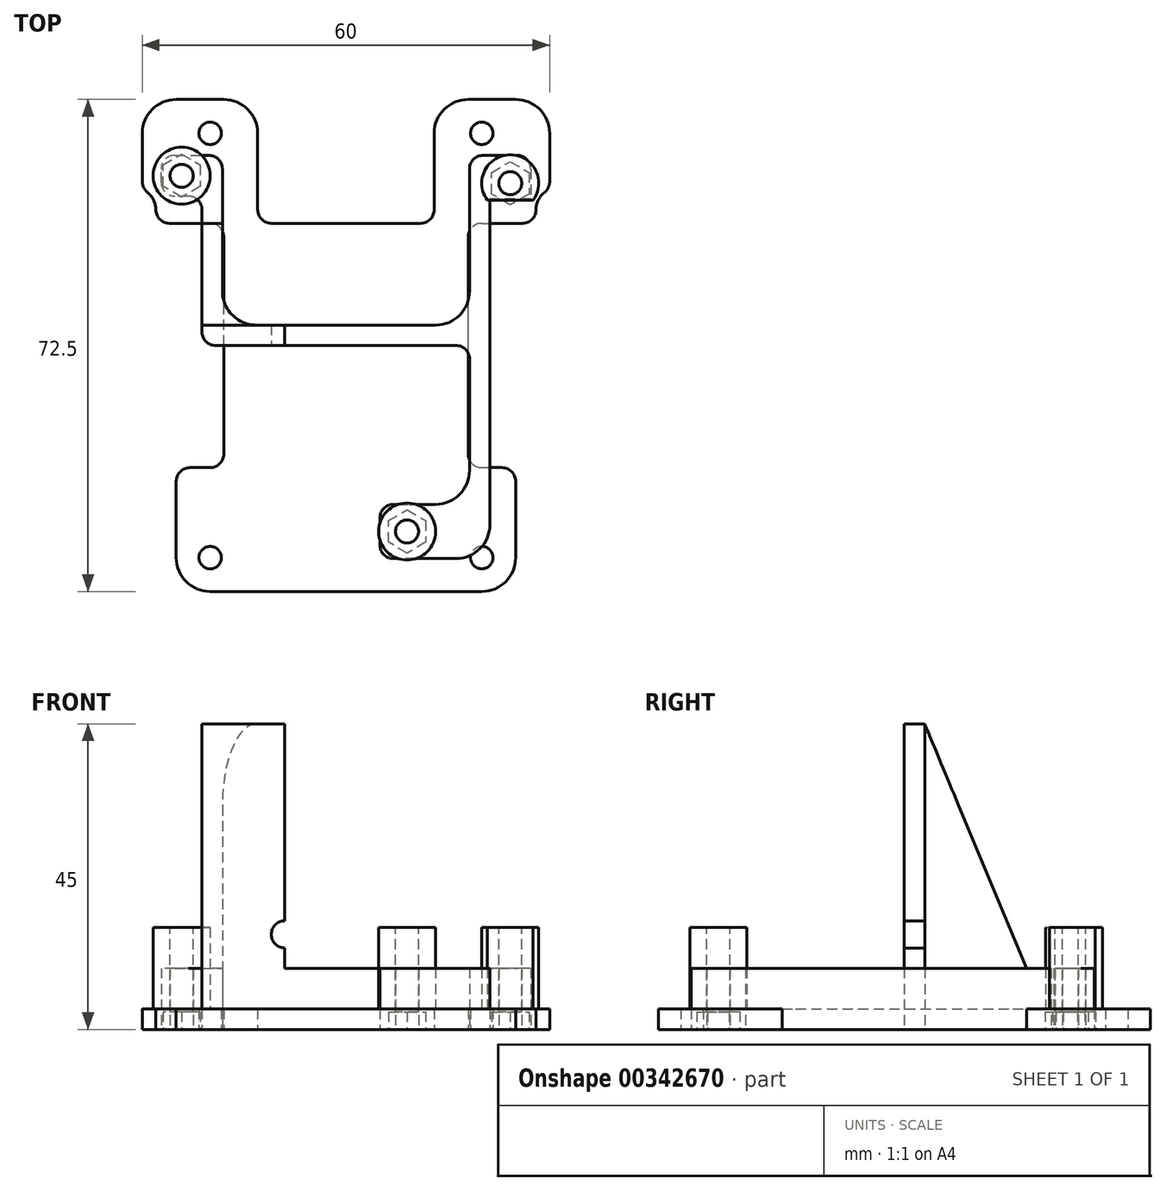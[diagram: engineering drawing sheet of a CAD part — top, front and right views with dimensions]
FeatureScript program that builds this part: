
annotation { "Feature Type Name" : "Feature", "Feature Type Description" : "" }
export const myFeature = defineFeature(function(context is Context, id is Id, definition is map)
    precondition{}
    {
        {
            var Q0;
            Q0=qCreatedBy(makeId("Top.planeOp"),FACE);
            var sketch = newSketch(context, id + "F0", { "sketchPlane" : qUnion([Q0])});
            skLineSegment(sketch, "E0.bottom", {"start": v(-35, -30) * mm, "end": v(35, -30) * mm, "construction": true});
            skLineSegment(sketch, "E0.top", {"start": v(-35, 52.5) * mm, "end": v(35, 52.5) * mm, "construction": true});
            skLineSegment(sketch, "E0.left", {"start": v(-35, -30) * mm, "end": v(-35, 52.5) * mm, "construction": true});
            skLineSegment(sketch, "E0.right", {"start": v(35, -30) * mm, "end": v(35, 52.5) * mm, "construction": true});
            skLineSegment(sketch, "E1", {"start": v(-35, 0) * mm, "end": v(35, 0) * mm, "construction": true});
            skCircle(sketch, "E2", {"center": v(-24.2, 25) * mm, "radius": 1.7 * mm});
            skCircle(sketch, "E3", {"center": v(24.2, 23.9) * mm, "radius": 1.7 * mm});
            skCircle(sketch, "E4", {"center": v(9, -27.4) * mm, "radius": 1.7 * mm});
            skCircle(sketch, "E5", {"center": v(-24.2, 25) * mm, "radius": 2.75 * mm, "construction": true});
            skLineSegment(sketch, "E6.0", {"start": v(-26.95, 23.41) * mm, "end": v(-26.95, 26.59) * mm});
            skLineSegment(sketch, "E6.1", {"start": v(-26.95, 26.59) * mm, "end": v(-24.2, 28.18) * mm});
            skLineSegment(sketch, "E6.2", {"start": v(-24.2, 28.18) * mm, "end": v(-21.45, 26.59) * mm});
            skLineSegment(sketch, "E6.3", {"start": v(-21.45, 26.59) * mm, "end": v(-21.45, 23.41) * mm});
            skLineSegment(sketch, "E6.4", {"start": v(-21.45, 23.41) * mm, "end": v(-24.2, 21.82) * mm});
            skLineSegment(sketch, "E6.5", {"start": v(-24.2, 21.82) * mm, "end": v(-26.95, 23.41) * mm});
            skPoint(sketch, "E6.0.midPoint", {"position": v(-26.95, 25) * mm});
            skCircle(sketch, "E7", {"center": v(24.2, 23.9) * mm, "radius": 2.75 * mm, "construction": true});
            skCircle(sketch, "E8", {"center": v(9, -27.4) * mm, "radius": 2.75 * mm, "construction": true});
            skLineSegment(sketch, "E9.0", {"start": v(26.95, 25.49) * mm, "end": v(26.95, 22.31) * mm});
            skLineSegment(sketch, "E9.1", {"start": v(26.95, 22.31) * mm, "end": v(24.2, 20.72) * mm});
            skLineSegment(sketch, "E9.2", {"start": v(24.2, 20.72) * mm, "end": v(21.45, 22.31) * mm});
            skLineSegment(sketch, "E9.3", {"start": v(21.45, 22.31) * mm, "end": v(21.45, 25.49) * mm});
            skLineSegment(sketch, "E9.4", {"start": v(21.45, 25.49) * mm, "end": v(24.2, 27.08) * mm});
            skLineSegment(sketch, "E9.5", {"start": v(24.2, 27.08) * mm, "end": v(26.95, 25.49) * mm});
            skPoint(sketch, "E9.0.midPoint", {"position": v(26.95, 23.9) * mm});
            skLineSegment(sketch, "E10.0", {"start": v(11.75, -25.81) * mm, "end": v(11.75, -28.99) * mm});
            skLineSegment(sketch, "E10.1", {"start": v(11.75, -28.99) * mm, "end": v(9, -30.58) * mm});
            skLineSegment(sketch, "E10.2", {"start": v(9, -30.58) * mm, "end": v(6.25, -28.99) * mm});
            skLineSegment(sketch, "E10.3", {"start": v(6.25, -28.99) * mm, "end": v(6.25, -25.81) * mm});
            skLineSegment(sketch, "E10.4", {"start": v(6.25, -25.81) * mm, "end": v(9, -24.22) * mm});
            skLineSegment(sketch, "E10.5", {"start": v(9, -24.22) * mm, "end": v(11.75, -25.81) * mm});
            skPoint(sketch, "E10.0.midPoint", {"position": v(11.75, -27.4) * mm});
            skSolve(sketch);
        }
        {
            var Q0;
            Q0=qCreatedBy(makeId("Top.planeOp"),FACE);
            var sketch = newSketch(context, id + "F1", { "sketchPlane" : qUnion([Q0])});
            skLineSegment(sketch, "E11.bottom", {"start": v(-20, -31.25) * mm, "end": v(20, -31.25) * mm, "construction": true});
            skLineSegment(sketch, "E11.top", {"start": v(-20, 31.25) * mm, "end": v(20, 31.25) * mm, "construction": true});
            skLineSegment(sketch, "E11.left", {"start": v(-20, -31.25) * mm, "end": v(-20, 31.25) * mm, "construction": true});
            skLineSegment(sketch, "E11.right", {"start": v(20, -31.25) * mm, "end": v(20, 31.25) * mm, "construction": true});
            skLineSegment(sketch, "E12", {"start": v(0, 31.25) * mm, "end": v(0, -31.25) * mm, "construction": true});
            skCircle(sketch, "E13", {"center": v(-20, 31.25) * mm, "radius": 1.65 * mm});
            skCircle(sketch, "E14", {"center": v(20, 31.25) * mm, "radius": 1.65 * mm});
            skCircle(sketch, "E15", {"center": v(20, -31.25) * mm, "radius": 1.65 * mm});
            skCircle(sketch, "E16", {"center": v(-20, -31.25) * mm, "radius": 1.65 * mm});
            skLineSegment(sketch, "E17.0", {"start": v(-25, -31.25) * mm, "end": v(-25, -20) * mm});
            skLineSegment(sketch, "E17.1", {"start": v(-20, -36.25) * mm, "end": v(20, -36.25) * mm});
            skLineSegment(sketch, "E17.2", {"start": v(25, -31.25) * mm, "end": v(25, -20) * mm});
            skLineSegment(sketch, "E17.3", {"start": v(-20, 36.25) * mm, "end": v(-18, 36.25) * mm});
            skPoint(sketch, "E18.visualSharp", {"position": v(25, -36.25) * mm});
            skArc(sketch, "E18.filletArc", {"start": v(20, -36.25) * mm, "mid": v(23.54, -34.79) * mm, "end": v(25, -31.25) * mm});
            skPoint(sketch, "E19.visualSharp", {"position": v(-25, -36.25) * mm});
            skArc(sketch, "E19.filletArc", {"start": v(-25, -31.25) * mm, "mid": v(-23.54, -34.79) * mm, "end": v(-20, -36.25) * mm});
            skCircle(sketch, "E20.0", {"center": v(-24.2, 25) * mm, "radius": 1.7 * mm, "construction": true});
            skCircle(sketch, "E21.0", {"center": v(24.2, 23.9) * mm, "radius": 1.7 * mm, "construction": true});
            skLineSegment(sketch, "E22.left", {"start": v(-18, -16) * mm, "end": v(-18, 16) * mm});
            skLineSegment(sketch, "E22.right", {"start": v(18, -16) * mm, "end": v(18, 16) * mm});
            skLineSegment(sketch, "E23", {"start": v(20, 18) * mm, "end": v(26, 18) * mm});
            skLineSegment(sketch, "E24", {"start": v(-20, -18) * mm, "end": v(-23, -18) * mm});
            skLineSegment(sketch, "E25", {"start": v(20, -18) * mm, "end": v(23, -18) * mm});
            skLineSegment(sketch, "E26", {"start": v(-18, 0) * mm, "end": v(18, 0) * mm, "construction": true});
            skPoint(sketch, "E27.visualSharp", {"position": v(-18, 18) * mm});
            skArc(sketch, "E27.filletArc", {"start": v(-18, 16) * mm, "mid": v(-18.59, 17.41) * mm, "end": v(-20, 18) * mm});
            skPoint(sketch, "E28.visualSharp", {"position": v(-18, -18) * mm});
            skArc(sketch, "E28.filletArc", {"start": v(-20, -18) * mm, "mid": v(-18.59, -17.41) * mm, "end": v(-18, -16) * mm});
            skPoint(sketch, "E29.visualSharp", {"position": v(-25, -18) * mm});
            skArc(sketch, "E29.filletArc", {"start": v(-23, -18) * mm, "mid": v(-24.41, -18.59) * mm, "end": v(-25, -20) * mm});
            skPoint(sketch, "E30.visualSharp", {"position": v(18, -18) * mm});
            skArc(sketch, "E30.filletArc", {"start": v(18, -16) * mm, "mid": v(18.59, -17.41) * mm, "end": v(20, -18) * mm});
            skPoint(sketch, "E31.visualSharp", {"position": v(25, -18) * mm});
            skArc(sketch, "E31.filletArc", {"start": v(25, -20) * mm, "mid": v(24.41, -18.59) * mm, "end": v(23, -18) * mm});
            skPoint(sketch, "E32.visualSharp", {"position": v(18, 18) * mm});
            skArc(sketch, "E32.filletArc", {"start": v(20, 18) * mm, "mid": v(18.59, 17.41) * mm, "end": v(18, 16) * mm});
            skLineSegment(sketch, "E33", {"start": v(-11, 18) * mm, "end": v(11, 18) * mm});
            skLineSegment(sketch, "E34", {"start": v(13, 20) * mm, "end": v(13, 31.25) * mm});
            skLineSegment(sketch, "E35", {"start": v(-13, 20) * mm, "end": v(-13, 31.25) * mm});
            skLineSegment(sketch, "E36.trimOffspring", {"start": v(18, 36.25) * mm, "end": v(25, 36.25) * mm});
            skPoint(sketch, "E37.visualSharp", {"position": v(-13, 36.25) * mm});
            skArc(sketch, "E37.filletArc", {"start": v(-13, 31.25) * mm, "mid": v(-14.46, 34.79) * mm, "end": v(-18, 36.25) * mm});
            skPoint(sketch, "E38.visualSharp", {"position": v(-13, 18) * mm});
            skArc(sketch, "E38.filletArc", {"start": v(-13, 20) * mm, "mid": v(-12.41, 18.59) * mm, "end": v(-11, 18) * mm});
            skPoint(sketch, "E39.visualSharp", {"position": v(13, 18) * mm});
            skArc(sketch, "E39.filletArc", {"start": v(11, 18) * mm, "mid": v(12.41, 18.59) * mm, "end": v(13, 20) * mm});
            skPoint(sketch, "E40.visualSharp", {"position": v(13, 36.25) * mm});
            skArc(sketch, "E40.filletArc", {"start": v(18, 36.25) * mm, "mid": v(14.46, 34.79) * mm, "end": v(13, 31.25) * mm});
            skLineSegment(sketch, "E41", {"start": v(30, 24.12) * mm, "end": v(30, 31.25) * mm});
            skLineSegment(sketch, "E42.MirrorCS", {"start": v(-20, 18) * mm, "end": v(-26, 18) * mm});
            skLineSegment(sketch, "E43.MirrorCS", {"start": v(-30, 24.12) * mm, "end": v(-30, 31.25) * mm});
            skLineSegment(sketch, "E44.MirrorCS", {"start": v(-18, 36.25) * mm, "end": v(-25, 36.25) * mm});
            skPoint(sketch, "E45.visualSharp", {"position": v(-30, 36.25) * mm});
            skArc(sketch, "E45.filletArc", {"start": v(-25, 36.25) * mm, "mid": v(-28.54, 34.79) * mm, "end": v(-30, 31.25) * mm});
            skPoint(sketch, "E46.visualSharp", {"position": v(30, 36.25) * mm});
            skArc(sketch, "E46.filletArc", {"start": v(30, 31.25) * mm, "mid": v(28.54, 34.79) * mm, "end": v(25, 36.25) * mm});
            skPoint(sketch, "E47.visualSharp", {"position": v(30, 18) * mm});
            skPoint(sketch, "E48.visualSharp", {"position": v(-30, 18) * mm});
            skLineSegment(sketch, "E49", {"start": v(0, 0) * mm, "end": v(11.31, 11.31) * mm, "construction": true});
            skCircle(sketch, "E50.MirrorC", {"center": v(31.25, 20) * mm, "radius": 1.65 * mm, "construction": true});
            skArc(sketch, "E51", {"start": v(29.24, 22.55) * mm, "mid": v(28.33, 21.42) * mm, "end": v(28, 20) * mm});
            skArc(sketch, "E52.MirrorC", {"start": v(-29.24, 22.55) * mm, "mid": v(-28.33, 21.42) * mm, "end": v(-28, 20) * mm});
            skPoint(sketch, "E53.visualSharp", {"position": v(-28.69, 18) * mm});
            skArc(sketch, "E53.filletArc", {"start": v(-28, 20) * mm, "mid": v(-27.41, 18.59) * mm, "end": v(-26, 18) * mm});
            skPoint(sketch, "E54.visualSharp", {"position": v(-30, 23) * mm});
            skArc(sketch, "E54.filletArc", {"start": v(-30, 24.12) * mm, "mid": v(-29.8, 23.25) * mm, "end": v(-29.24, 22.55) * mm});
            skPoint(sketch, "E55.visualSharp", {"position": v(28.69, 18) * mm});
            skArc(sketch, "E55.filletArc", {"start": v(26, 18) * mm, "mid": v(27.41, 18.59) * mm, "end": v(28, 20) * mm});
            skPoint(sketch, "E56.visualSharp", {"position": v(30, 23) * mm});
            skArc(sketch, "E56.filletArc", {"start": v(29.24, 22.55) * mm, "mid": v(29.8, 23.25) * mm, "end": v(30, 24.12) * mm});
            skSolve(sketch);
        }
        {
            var Q0;
            Q0 = qSketchRegion(id + "F1", true);
            extrude(context, id + "F2", {"entities" : qUnion([Q0]), "depth" : 3 * mm});
        }
        {
            var Q0;
            Q0=makeQuery(id+"F2.opExtrude","CAP_FACE",FACE,{"disambiguationData":[OSD([sQuery(id+"F1.wireOp",EDGE,"E13"),sQuery(id+"F1.wireOp",EDGE,"E14"),sQuery(id+"F1.wireOp",EDGE,"E15"),sQuery(id+"F1.wireOp",EDGE,"E16"),sQuery(id+"F1.wireOp",EDGE,"E17.0"),sQuery(id+"F1.wireOp",EDGE,"E17.1"),sQuery(id+"F1.wireOp",EDGE,"E17.2"),sQuery(id+"F1.wireOp",EDGE,"E17.3"),sQuery(id+"F1.wireOp",EDGE,"870219dc-a750-4bc9-ad78-546a003762bf.filletArc"),sQuery(id+"F1.wireOp",EDGE,"cf5fab91-087c-4f74-afe7-adf2e257fd87.filletArc"),sQuery(id+"F1.wireOp",EDGE,"E18.filletArc"),sQuery(id+"F1.wireOp",EDGE,"E19.filletArc"),sQuery(id+"F1.wireOp",EDGE,"E22.left"),sQuery(id+"F1.wireOp",EDGE,"E22.right"),sQuery(id+"F1.wireOp",EDGE,"0aHINH7d-Yn7U-1H70-jHRU-5q84e7slqB47"),sQuery(id+"F1.wireOp",EDGE,"E23"),sQuery(id+"F1.wireOp",EDGE,"E24"),sQuery(id+"F1.wireOp",EDGE,"E25"),sQuery(id+"F1.wireOp",EDGE,"f18657db-0b7e-4821-ad0d-cfc5a41b6451.trimOffspring"),sQuery(id+"F1.wireOp",EDGE,"93d343bc-5fb2-4c8f-aaa1-3655ac94b7ac.trimOffspring"),sQuery(id+"F1.wireOp",EDGE,"66acb56a-2039-4175-9e05-3a058cd02a39.filletArc"),sQuery(id+"F1.wireOp",EDGE,"E27.filletArc"),sQuery(id+"F1.wireOp",EDGE,"E28.filletArc"),sQuery(id+"F1.wireOp",EDGE,"E29.filletArc"),sQuery(id+"F1.wireOp",EDGE,"E30.filletArc"),sQuery(id+"F1.wireOp",EDGE,"E31.filletArc"),sQuery(id+"F1.wireOp",EDGE,"E32.filletArc"),sQuery(id+"F1.wireOp",EDGE,"a8163136-e520-4838-bb3d-139567249151.filletArc")])],"isStart":false});
            var sketch = newSketch(context, id + "F3", { "sketchPlane" : qUnion([Q0])});
            skCircle(sketch, "E57.0", {"center": v(-24.2, 25) * mm, "radius": 1.7 * mm, "construction": true});
            skCircle(sketch, "E58.0", {"center": v(24.2, 23.9) * mm, "radius": 1.7 * mm, "construction": true});
            skCircle(sketch, "E59.0", {"center": v(9, -27.4) * mm, "radius": 1.7 * mm, "construction": true});
            skArc(sketch, "E60.0", {"start": v(27.57, 21.4) * mm, "mid": v(24.2, 28.1) * mm, "end": v(20.83, 21.4) * mm});
            skCircle(sketch, "E61.0", {"center": v(9, -27.4) * mm, "radius": 4.2 * mm});
            skLineSegment(sketch, "E62", {"start": v(20.83, 21.4) * mm, "end": v(27.57, 21.4) * mm});
            skPoint(sketch, "E63.orphan", {"position": v(30.13, 21.4) * mm});
            skCircle(sketch, "E64.0", {"center": v(-24.2, 25) * mm, "radius": 4.2 * mm});
            skSolve(sketch);
        }
        {
            var Q0;
            Q0 = qSketchRegion(id + "F3", true);
            extrude(context, id + "F4", {"entities" : qUnion([Q0]), "operationType" : NewBodyOperationType.ADD, "depth" : 12 * mm});
        }
        {
            var Q0;
            Q0=makeQuery(id+"F4.opExtrude","CAP_FACE",FACE,{"disambiguationData":[OSD([sQuery(id+"F3.wireOp",EDGE,"E64.0")])],"isStart":false});
            var sketch = newSketch(context, id + "F5", { "sketchPlane" : qUnion([Q0])});
            skCircle(sketch, "E65.0", {"center": v(-24.2, 25) * mm, "radius": 1.7 * mm});
            skCircle(sketch, "E66.0", {"center": v(24.2, 23.9) * mm, "radius": 1.7 * mm});
            skCircle(sketch, "E67.0", {"center": v(9, -27.4) * mm, "radius": 1.7 * mm});
            skSolve(sketch);
        }
        {
            var Q0;
            Q0 = qSketchRegion(id + "F5", true);
            extrude(context, id + "F6", {"entities" : qUnion([Q0]), "operationType" : NewBodyOperationType.REMOVE, "endBound" : BoundingType.THROUGH_ALL, "oppositeDirection" : true, "depth" : 25 * mm});
        }
        {
            var Q0;
            Q0 = qSketchRegion(id + "F0", true);
            extrude(context, id + "F7", {"entities" : qUnion([Q0]), "operationType" : NewBodyOperationType.REMOVE, "depth" : 2.6 * mm});
        }
        {
            var Q0;
            Q0=qCreatedBy(makeId("Top.planeOp"),FACE);
            var sketch = newSketch(context, id + "F8", { "sketchPlane" : qUnion([Q0])});
            skCircle(sketch, "E68.0", {"center": v(-24.2, 25) * mm, "radius": 1.7 * mm});
            skCircle(sketch, "E69.0", {"center": v(24.2, 23.9) * mm, "radius": 1.7 * mm});
            skCircle(sketch, "E70.0", {"center": v(9, -27.4) * mm, "radius": 1.7 * mm});
            skLineSegment(sketch, "E71", {"start": v(-19.2, 0) * mm, "end": v(16.2, 0) * mm});
            skLineSegment(sketch, "E72", {"start": v(-21.2, 2) * mm, "end": v(-21.2, 20) * mm});
            skLineSegment(sketch, "E73", {"start": v(-23.2, 22) * mm, "end": v(-25.2, 22) * mm});
            skLineSegment(sketch, "E74", {"start": v(-27.2, 24) * mm, "end": v(-27.2, 26) * mm});
            skLineSegment(sketch, "E75", {"start": v(-25.2, 28) * mm, "end": v(-20.2, 28) * mm});
            skLineSegment(sketch, "E76", {"start": v(-18.2, 26) * mm, "end": v(-18.2, 18.81) * mm});
            skLineSegment(sketch, "E77", {"start": v(-18.2, 18.81) * mm, "end": v(-18.2, 8) * mm});
            skLineSegment(sketch, "E78", {"start": v(-13.2, 3) * mm, "end": v(13.2, 3) * mm});
            skLineSegment(sketch, "E79", {"start": v(18.2, 8) * mm, "end": v(18.2, 26) * mm});
            skLineSegment(sketch, "E80", {"start": v(20.2, 28) * mm, "end": v(25.2, 28) * mm});
            skLineSegment(sketch, "E81", {"start": v(27.2, 26) * mm, "end": v(27.2, 21.6) * mm});
            skLineSegment(sketch, "E82", {"start": v(27.2, 21.6) * mm, "end": v(21.2, 21.6) * mm});
            skLineSegment(sketch, "E83", {"start": v(21.2, 21.6) * mm, "end": v(21.2, -26.4) * mm});
            skLineSegment(sketch, "E84", {"start": v(16.2, -31.4) * mm, "end": v(7, -31.4) * mm});
            skLineSegment(sketch, "E85", {"start": v(5, -29.4) * mm, "end": v(5, -25.4) * mm});
            skLineSegment(sketch, "E86", {"start": v(7, -23.4) * mm, "end": v(13.2, -23.4) * mm});
            skLineSegment(sketch, "E87", {"start": v(18.2, -18.4) * mm, "end": v(18.2, -2) * mm});
            skLineSegment(sketch, "E88", {"start": v(10, 6.3) * mm, "end": v(10, -7.37) * mm, "construction": true});
            skLineSegment(sketch, "E89", {"start": v(-18, 8.77) * mm, "end": v(-18, -6.78) * mm, "construction": true});
            skPoint(sketch, "E90.visualSharp", {"position": v(18.2, -23.4) * mm});
            skArc(sketch, "E90.filletArc", {"start": v(13.2, -23.4) * mm, "mid": v(16.74, -21.94) * mm, "end": v(18.2, -18.4) * mm});
            skPoint(sketch, "E91.visualSharp", {"position": v(18.2, 3) * mm});
            skArc(sketch, "E91.filletArc", {"start": v(13.2, 3) * mm, "mid": v(16.74, 4.46) * mm, "end": v(18.2, 8) * mm});
            skPoint(sketch, "E92.visualSharp", {"position": v(-18.2, 3) * mm});
            skArc(sketch, "E92.filletArc", {"start": v(-18.2, 8) * mm, "mid": v(-16.74, 4.46) * mm, "end": v(-13.2, 3) * mm});
            skPoint(sketch, "E93.visualSharp", {"position": v(21.2, -31.4) * mm});
            skArc(sketch, "E93.filletArc", {"start": v(16.2, -31.4) * mm, "mid": v(19.74, -29.94) * mm, "end": v(21.2, -26.4) * mm});
            skPoint(sketch, "E94.visualSharp", {"position": v(18.2, 28) * mm});
            skArc(sketch, "E94.filletArc", {"start": v(20.2, 28) * mm, "mid": v(18.79, 27.41) * mm, "end": v(18.2, 26) * mm});
            skPoint(sketch, "E95.visualSharp", {"position": v(27.2, 28) * mm});
            skArc(sketch, "E95.filletArc", {"start": v(27.2, 26) * mm, "mid": v(26.61, 27.41) * mm, "end": v(25.2, 28) * mm});
            skPoint(sketch, "E96.visualSharp", {"position": v(-18.2, 28) * mm});
            skArc(sketch, "E96.filletArc", {"start": v(-18.2, 26) * mm, "mid": v(-18.79, 27.41) * mm, "end": v(-20.2, 28) * mm});
            skPoint(sketch, "E97.visualSharp", {"position": v(-27.2, 22) * mm});
            skArc(sketch, "E97.filletArc", {"start": v(-27.2, 24) * mm, "mid": v(-26.61, 22.59) * mm, "end": v(-25.2, 22) * mm});
            skPoint(sketch, "E98.visualSharp", {"position": v(-21.2, 22) * mm});
            skArc(sketch, "E98.filletArc", {"start": v(-21.2, 20) * mm, "mid": v(-21.79, 21.41) * mm, "end": v(-23.2, 22) * mm});
            skPoint(sketch, "E99.visualSharp", {"position": v(-21.2, 0) * mm});
            skArc(sketch, "E99.filletArc", {"start": v(-21.2, 2) * mm, "mid": v(-20.61, 0.59) * mm, "end": v(-19.2, 0) * mm});
            skPoint(sketch, "E100.visualSharp", {"position": v(5, -23.4) * mm});
            skArc(sketch, "E100.filletArc", {"start": v(7, -23.4) * mm, "mid": v(5.59, -23.99) * mm, "end": v(5, -25.4) * mm});
            skPoint(sketch, "E101.visualSharp", {"position": v(5, -31.4) * mm});
            skArc(sketch, "E101.filletArc", {"start": v(5, -29.4) * mm, "mid": v(5.59, -30.81) * mm, "end": v(7, -31.4) * mm});
            skPoint(sketch, "E102.visualSharp", {"position": v(-27.2, 28) * mm});
            skArc(sketch, "E102.filletArc", {"start": v(-25.2, 28) * mm, "mid": v(-26.61, 27.41) * mm, "end": v(-27.2, 26) * mm});
            skPoint(sketch, "E103.visualSharp", {"position": v(18.2, 0) * mm});
            skArc(sketch, "E103.filletArc", {"start": v(18.2, -2) * mm, "mid": v(17.61, -0.59) * mm, "end": v(16.2, 0) * mm});
            skSolve(sketch);
        }
        {
            var Q0;
            Q0 = qSketchRegion(id + "F8", true);
            extrude(context, id + "F9", {"entities" : qUnion([Q0]), "depth" : 9 * mm});
        }
        {
            var Q0;
            Q0=makeQuery(id+"F9.opExtrude","CAP_FACE",FACE,{"disambiguationData":[OSD([sQuery(id+"F8.wireOp",EDGE,"E68.0"),sQuery(id+"F8.wireOp",EDGE,"E69.0"),sQuery(id+"F8.wireOp",EDGE,"E70.0"),sQuery(id+"F8.wireOp",EDGE,"E71"),sQuery(id+"F8.wireOp",EDGE,"E72"),sQuery(id+"F8.wireOp",EDGE,"E73"),sQuery(id+"F8.wireOp",EDGE,"E74"),sQuery(id+"F8.wireOp",EDGE,"E75"),sQuery(id+"F8.wireOp",EDGE,"E76"),sQuery(id+"F8.wireOp",EDGE,"E77"),sQuery(id+"F8.wireOp",EDGE,"E78"),sQuery(id+"F8.wireOp",EDGE,"E79"),sQuery(id+"F8.wireOp",EDGE,"E80"),sQuery(id+"F8.wireOp",EDGE,"E81"),sQuery(id+"F8.wireOp",EDGE,"E82"),sQuery(id+"F8.wireOp",EDGE,"E83"),sQuery(id+"F8.wireOp",EDGE,"E84"),sQuery(id+"F8.wireOp",EDGE,"E85"),sQuery(id+"F8.wireOp",EDGE,"E86"),sQuery(id+"F8.wireOp",EDGE,"E87"),sQuery(id+"F8.wireOp",EDGE,"E90.filletArc"),sQuery(id+"F8.wireOp",EDGE,"E91.filletArc"),sQuery(id+"F8.wireOp",EDGE,"E92.filletArc"),sQuery(id+"F8.wireOp",EDGE,"E93.filletArc"),sQuery(id+"F8.wireOp",EDGE,"E94.filletArc"),sQuery(id+"F8.wireOp",EDGE,"E95.filletArc"),sQuery(id+"F8.wireOp",EDGE,"E96.filletArc"),sQuery(id+"F8.wireOp",EDGE,"E97.filletArc"),sQuery(id+"F8.wireOp",EDGE,"E98.filletArc"),sQuery(id+"F8.wireOp",EDGE,"E99.filletArc"),sQuery(id+"F8.wireOp",EDGE,"E100.filletArc"),sQuery(id+"F8.wireOp",EDGE,"E101.filletArc"),sQuery(id+"F8.wireOp",EDGE,"E102.filletArc"),sQuery(id+"F8.wireOp",EDGE,"E103.filletArc")])],"isStart":false});
            var sketch = newSketch(context, id + "F10", { "sketchPlane" : qUnion([Q0])});
            skLineSegment(sketch, "E104", {"start": v(-17, 13.86) * mm, "end": v(-17, -10.58) * mm, "construction": true});
            skLineSegment(sketch, "E105", {"start": v(11, -8.66) * mm, "end": v(11, 12.1) * mm, "construction": true});
            skLineSegment(sketch, "E106", {"start": v(-9, 3) * mm, "end": v(-9, 0) * mm});
            skLineSegment(sketch, "E107", {"start": v(-9, 0) * mm, "end": v(-19.2, 0) * mm});
            skLineSegment(sketch, "E108", {"start": v(-21.2, 2) * mm, "end": v(-21.2, 18) * mm});
            skLineSegment(sketch, "E109", {"start": v(-21.2, 18) * mm, "end": v(-18.2, 18) * mm});
            skLineSegment(sketch, "E110.0", {"start": v(-18.2, 18) * mm, "end": v(-18.2, 8) * mm});
            skArc(sketch, "E111.0", {"start": v(-18.2, 8) * mm, "mid": v(-16.74, 4.46) * mm, "end": v(-13.2, 3) * mm});
            skLineSegment(sketch, "E112.0", {"start": v(-13.2, 3) * mm, "end": v(-9, 3) * mm});
            skPoint(sketch, "E113.orphan", {"position": v(-18.2, 18.81) * mm});
            skPoint(sketch, "E114.orphan", {"position": v(-9, 5.09) * mm});
            skArc(sketch, "E115.0", {"start": v(-21.2, 2) * mm, "mid": v(-20.61, 0.59) * mm, "end": v(-19.2, 0) * mm});
            skPoint(sketch, "E116.orphan", {"position": v(-21.2, 0) * mm});
            skSolve(sketch);
        }
        {
            var Q0;
            Q0 = qSketchRegion(id + "F10", true);
            extrude(context, id + "F11", {"entities" : qUnion([Q0]), "operationType" : NewBodyOperationType.ADD, "depth" : 36 * mm});
        }
        {
            var Q0;
            Q0=makeQuery(id+"F11.boolean.opBoolean","MERGE",FACE,{"derivedFrom":[makeQuery(id+"F9.opExtrude","SWEPT_FACE",FACE,{"disambiguationData":[OSD([sQuery(id+"F8.wireOp",EDGE,"E71")])]}),makeQuery(id+"F11.opExtrude","SWEPT_FACE",FACE,{"disambiguationData":[OSD([sQuery(id+"F10.wireOp",EDGE,"xUDsLxzo-tMbO-FFqX-LzO3-AvgrbZf4334z.bottom")])]})]});
            var sketch = newSketch(context, id + "F12", { "sketchPlane" : qUnion([Q0])});
            skLineSegment(sketch, "E117", {"start": v(0, 0) * mm, "end": v(0, 45) * mm, "construction": true});
            skLineSegment(sketch, "E118.bottom", {"start": v(11, 45) * mm, "end": v(-17, 45) * mm, "construction": true});
            skLineSegment(sketch, "E118.top", {"start": v(11, 2) * mm, "end": v(-17, 2) * mm, "construction": true});
            skLineSegment(sketch, "E118.left", {"start": v(11, 45) * mm, "end": v(11, 2) * mm, "construction": true});
            skLineSegment(sketch, "E118.right", {"start": v(-17, 45) * mm, "end": v(-17, 2) * mm, "construction": true});
            skCircle(sketch, "E119", {"center": v(-9, 14) * mm, "radius": 2 * mm});
            skSolve(sketch);
        }
        {
            var Q0;
            Q0 = qSketchRegion(id + "F12", true);
            extrude(context, id + "F13", {"entities" : qUnion([Q0]), "operationType" : NewBodyOperationType.REMOVE, "endBound" : BoundingType.THROUGH_ALL, "oppositeDirection" : true, "depth" : 25 * mm});
        }
        {
            var Q0;
            Q0=makeQuery(id+"F11.opExtrude","CAP_EDGE",EDGE,{"disambiguationData":[OSD([sQuery(id+"F10.wireOp",EDGE,"E109")])],"isStart":false});
            chamfer(context, id + "F14", {"entities" : qUnion([Q0]), "chamferType" : ChamferType.TWO_OFFSETS, "width1" : 36 * mm, "oppositeDirection" : false, "width2" : 15 * mm, "tangentPropagation" : true});
        }
    });
